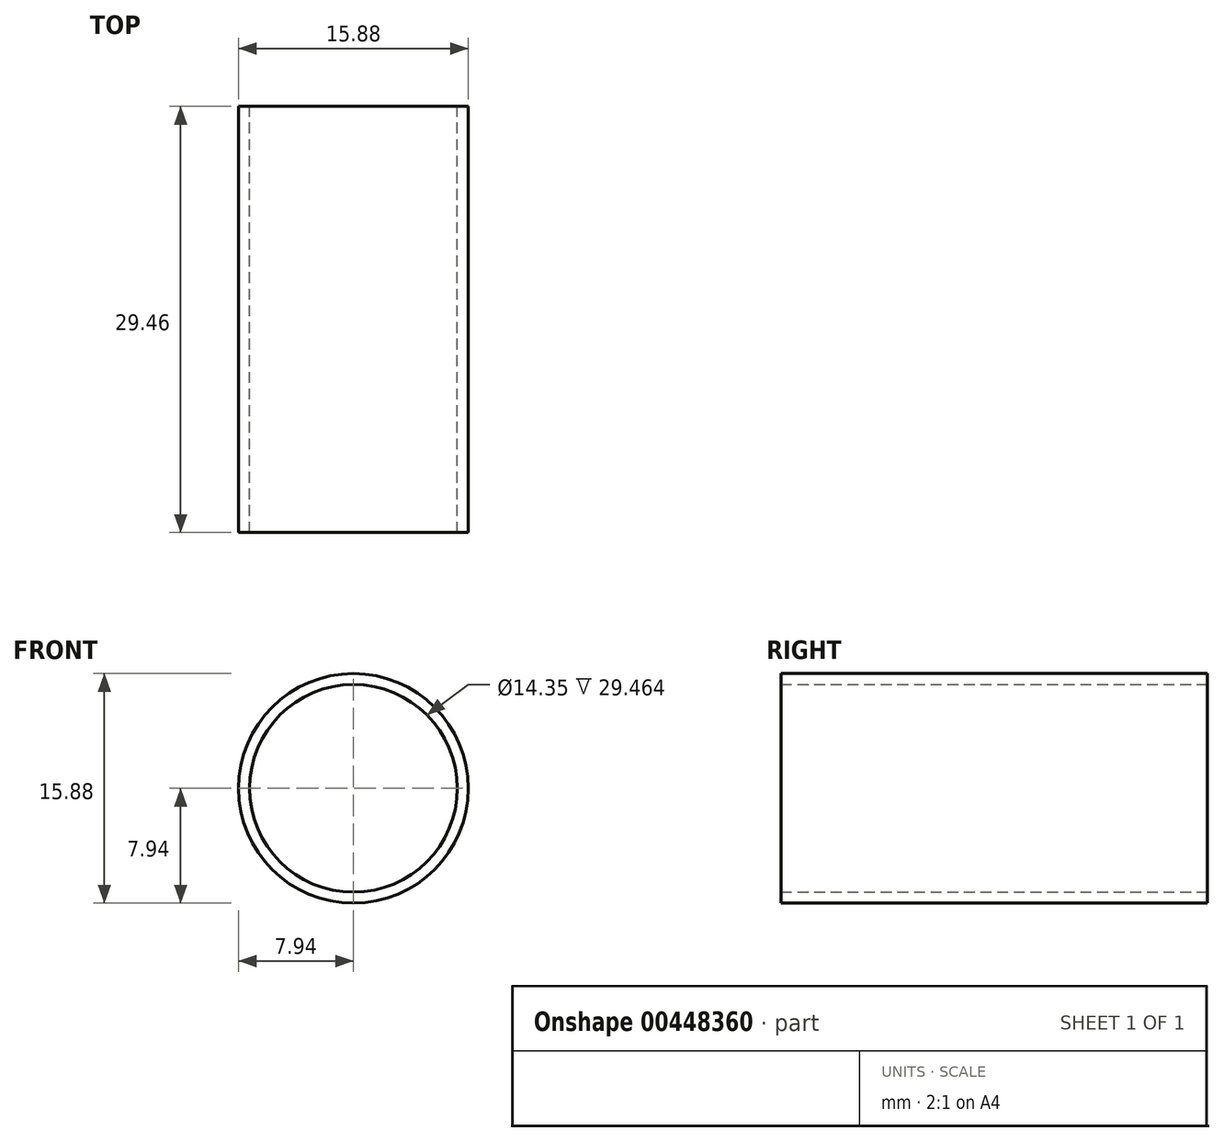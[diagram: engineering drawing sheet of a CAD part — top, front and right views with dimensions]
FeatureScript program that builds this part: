
annotation { "Feature Type Name" : "Feature", "Feature Type Description" : "" }
export const myFeature = defineFeature(function(context is Context, id is Id, definition is map)
    precondition{}
    {
        {
            var Q0;
            Q0=qCreatedBy(makeId("Front.planeOp"),FACE);
            var sketch = newSketch(context, id + "F0", { "sketchPlane" : qUnion([Q0])});
            skCircle(sketch, "E0", {"center": v(0, 0) * mm, "radius": 7.94 * mm});
            skCircle(sketch, "E1.0", {"center": v(0, 0) * mm, "radius": 7.18 * mm});
            skSolve(sketch);
        }
        {
            var Q0;
            Q0=makeQuery(id+"F0.imprint","IMPRINT",FACE,{"disambiguationData":[TD([[makeQuery(id+"F0.imprint","IMPRINT",EDGE,{"derivedFrom":sQuery(id+"F0.wireOp",EDGE,"E0")}),1.0]])]});
            extrude(context, id + "F1", {"entities" : qUnion([Q0]), "depth" : 29.46 * mm});
        }
    });
